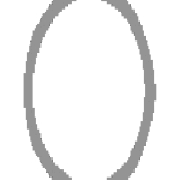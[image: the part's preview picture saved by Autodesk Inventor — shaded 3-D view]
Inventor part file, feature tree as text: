
AUTODESK INVENTOR PART (.ipt)
format: ipt  version: 2021 (Build 250183000, 183)  size: 126,464 bytes
history: native  units: in
note: dims shown in document units (in); Inventor stores cm internally (conversion verified against a paired STEP export)
features: other x4, plane x4, sketch x4, extrude x1, boolean_combine x1
ambient origin geometry x8: Origin, YZ Plane, XZ Plane, XY Plane, X Axis, Y Axis, Z Axis, Center Point
bodies: Solid1 (feature_tree), Body (feature_tree), Solid2 (feature_tree)
feature tree (14):
  other  "Driven Length"
  other  "Frame Generator"
  other  "Start Plane"
  other  "End Plane"
  plane  "Work Plane4"
  plane  "Work Plane5"
  plane  "Work Plane6"
  extrude  "Extrusion3"  Depth=0.065in
  boolean_combine  "Combine1"
  sketch  "Sketch"  dims[d5=23.8537in d6=0.12in d7=0.0in d8=90.0deg d9=23.8537in d10=0.12in d11=0.0in]
  sketch  "Sketch2"  dims[d0=1.0in d1=0.065in]
  plane  "Work Plane3"
  sketch  "Sketch3"  dims[d2=23.8537in]
  sketch  "Sketch4"  dims[d4=-0.0in]
